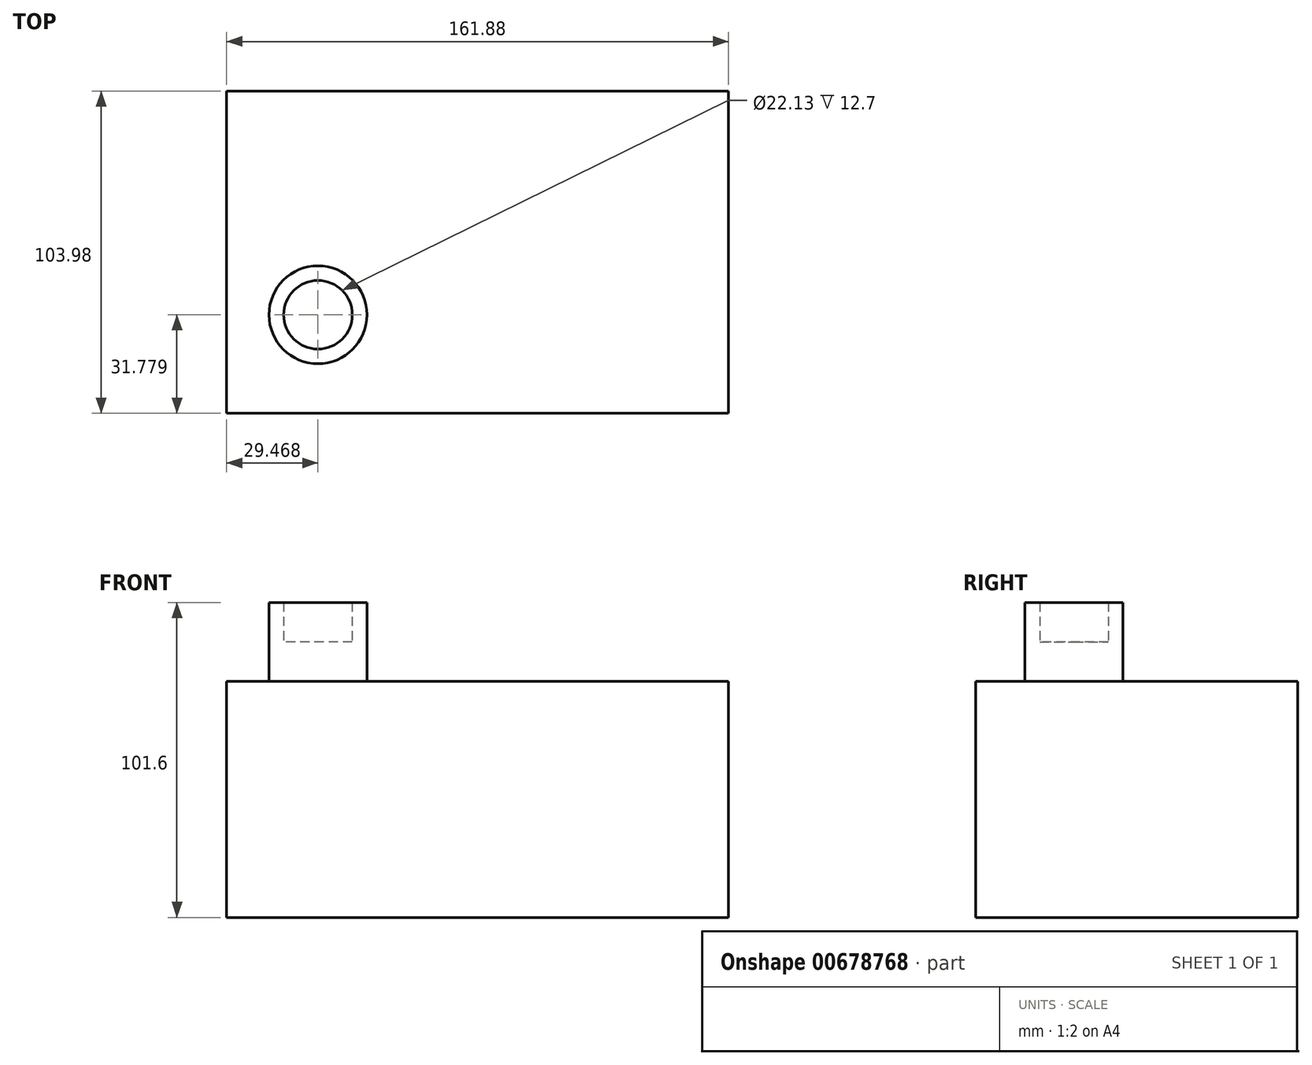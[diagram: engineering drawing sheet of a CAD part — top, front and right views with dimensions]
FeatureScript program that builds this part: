
annotation { "Feature Type Name" : "Feature", "Feature Type Description" : "" }
export const myFeature = defineFeature(function(context is Context, id is Id, definition is map)
    precondition{}
    {
        {
            var Q0;
            Q0=qCreatedBy(makeId("Top.planeOp"),FACE);
            var sketch = newSketch(context, id + "F0", { "sketchPlane" : qUnion([Q0])});
            skLineSegment(sketch, "E0.bottom", {"start": v(-80.94, 51.99) * mm, "end": v(80.94, 51.99) * mm});
            skLineSegment(sketch, "E0.top", {"start": v(-80.94, -51.99) * mm, "end": v(80.94, -51.99) * mm});
            skLineSegment(sketch, "E0.left", {"start": v(-80.94, 51.99) * mm, "end": v(-80.94, -51.99) * mm});
            skLineSegment(sketch, "E0.right", {"start": v(80.94, 51.99) * mm, "end": v(80.94, -51.99) * mm});
            skPoint(sketch, "E0.middle", {"position": v(0, 0) * mm});
            skSolve(sketch);
        }
        {
            var Q0;
            Q0 = qSketchRegion(id + "F0", true);
            extrude(context, id + "F1", {"entities" : qUnion([Q0]), "depth" : 76.2 * mm, "offsetDistance" : 25.4 * mm});
        }
        {
            var Q0;
            Q0=makeQuery(id+"F1.opExtrude","CAP_FACE",FACE,{"disambiguationData":[OSD([sQuery(id+"F0.wireOp",EDGE,"E0.bottom"),sQuery(id+"F0.wireOp",EDGE,"E0.top"),sQuery(id+"F0.wireOp",EDGE,"E0.left"),sQuery(id+"F0.wireOp",EDGE,"E0.right")])],"isStart":false});
            var sketch = newSketch(context, id + "F2", { "sketchPlane" : qUnion([Q0])});
            skCircle(sketch, "E1", {"center": v(-51.47, -20.21) * mm, "radius": 15.8 * mm});
            skSolve(sketch);
        }
        {
            var Q0;
            Q0 = qSketchRegion(id + "F2", true);
            extrude(context, id + "F3", {"entities" : qUnion([Q0]), "operationType" : NewBodyOperationType.ADD, "depth" : 25.4 * mm, "offsetDistance" : 25.4 * mm});
        }
        {
            var Q0;
            Q0=makeQuery(id+"F3.opExtrude","CAP_FACE",FACE,{"disambiguationData":[OSD([sQuery(id+"F2.wireOp",EDGE,"E1")])],"isStart":false});
            var sketch = newSketch(context, id + "F4", { "sketchPlane" : qUnion([Q0])});
            skCircle(sketch, "E2", {"center": v(-51.47, -20.21) * mm, "radius": 11.06 * mm});
            skSolve(sketch);
        }
        {
            var Q0;
            Q0 = qSketchRegion(id + "F4", true);
            extrude(context, id + "F5", {"entities" : qUnion([Q0]), "operationType" : NewBodyOperationType.REMOVE, "endBound" : BoundingType.SYMMETRIC, "depth" : -25.4 * mm, "offsetDistance" : 25.4 * mm});
        }
    });
